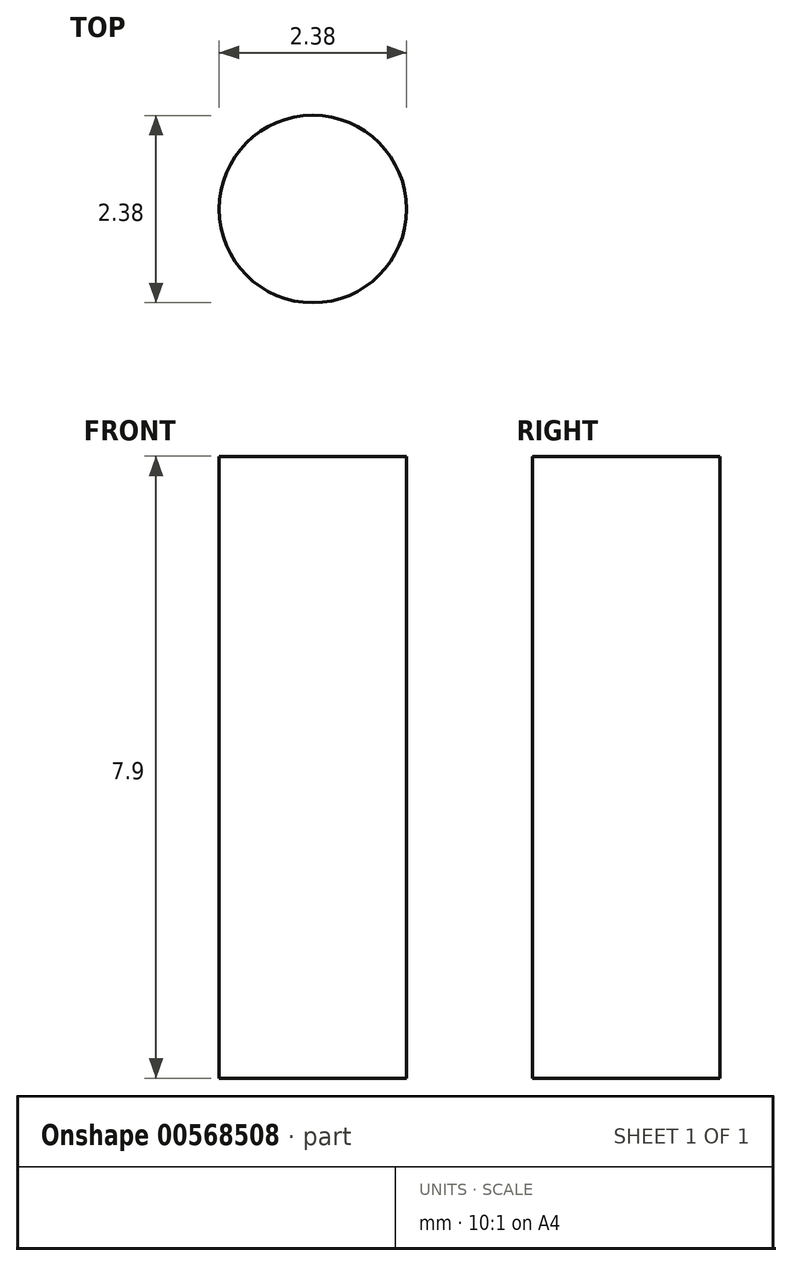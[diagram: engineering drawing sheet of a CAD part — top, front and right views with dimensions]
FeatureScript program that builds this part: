
annotation { "Feature Type Name" : "Feature", "Feature Type Description" : "" }
export const myFeature = defineFeature(function(context is Context, id is Id, definition is map)
    precondition{}
    {
        {
            var Q0;
            Q0=qCreatedBy(makeId("Top.planeOp"),FACE);
            var sketch = newSketch(context, id + "F0", { "sketchPlane" : qUnion([Q0])});
            skCircle(sketch, "E0", {"center": v(0, 0) * mm, "radius": 1.2 * mm});
            skSolve(sketch);
        }
        {
            var Q0;
            Q0 = qSketchRegion(id + "F0", true);
            extrude(context, id + "F1", {"entities" : qUnion([Q0]), "depth" : 7.9 * mm, "offsetDistance" : 25.4 * mm});
        }
    });
